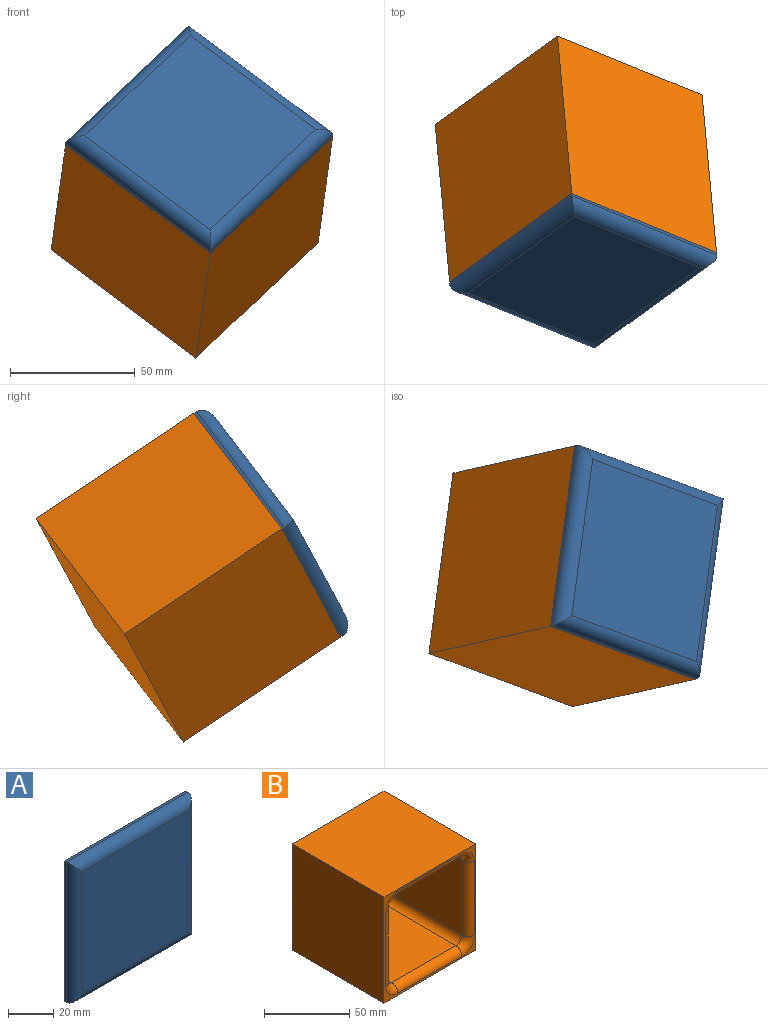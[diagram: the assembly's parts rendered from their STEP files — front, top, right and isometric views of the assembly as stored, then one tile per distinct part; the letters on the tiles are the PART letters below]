
ASSEMBLY  parts=2 mates=1
PART A: 10 faces, bbox 76.2x6.4x76.2 mm
  f0: plane 76.2x1.27mm, normal (0,0,-1), area 96.8mm2, adj f1,f3,f5,f6
  f1: plane 76.2x1.27mm, normal (1,0,0), area 96.8mm2, adj f0,f2,f5,f7
  f2: plane 76.2x1.27mm, normal (0,0,1), area 96.8mm2, adj f1,f3,f5,f9
  f3: plane 76.2x1.27mm, normal (-1,0,0), area 96.8mm2, adj f0,f2,f5,f8
  f4: plane 66.04x66.04mm, normal (0,-1,0), area 4361.3mm2, adj f6,f7,f8,f9
  f5: plane 76.2x76.2mm, normal (0,1,0), area 5806.4mm2, adj f0,f1,f2,f3
  f6: cylinder r=5.08mm len=76.2mm, axis (-1,0,0), area 578.6mm2, adj f0,f4,f7,f8
  f7: cylinder r=5.08mm len=76.2mm, axis (0,0,-1), area 578.6mm2, adj f1,f4,f6,f9
  f8: cylinder r=5.08mm len=76.2mm, axis (0,0,1), area 578.6mm2, adj f3,f4,f6,f9
  f9: cylinder r=5.08mm len=76.2mm, axis (1,0,0), area 578.6mm2, adj f2,f4,f7,f8
PART B: 31 faces, bbox 83.1x76.2x83.1 mm
  f0: plane 76.2x76.2mm, normal (0,-1,0), area 469.3mm2, adj f1,f2,f3,f4,f12,f15,f16,f19
  f1: plane 76.2x76.2mm, normal (1,0,0), area 5806.4mm2, adj f0,f2,f4,f5
  f2: plane 76.2x76.2mm, normal (0,0,1), area 5806.4mm2, adj f0,f1,f3,f5
  f3: plane 76.2x76.2mm, normal (-1,0,0), area 5806.4mm2, adj f0,f2,f4,f5
  f4: plane 76.2x76.2mm, normal (0,0,-1), area 5806.4mm2, adj f0,f1,f3,f5
  f5: plane 76.2x76.2mm, normal (0,1,0), area 5806.4mm2, adj f1,f2,f3,f4
  f6: plane 59.69x53.34mm, normal (0,0,1), area 3183.9mm2, adj f13,f17,f20,f21
  f7: plane 59.69x53.34mm, normal (-1,0,0), area 3183.9mm2, adj f18,f21,f24,f29
  f8: plane 59.69x53.34mm, normal (0,0,-1), area 3183.9mm2, adj f11,f14,f18,f19
  f9: plane 59.69x53.34mm, normal (1,0,0), area 3183.9mm2, adj f11,f12,f13,f26
  f10: plane 53.34x53.34mm, normal (0,-1,0), area 2845.2mm2, adj f14,f17,f26,f29
  f11: cylinder r=5.08mm len=59.69mm, axis (0,1,0), area 476.3mm2, adj f8,f9,f15,f27
  f12: cylinder r=5.08mm len=53.34mm, axis (0,0,1), area 425.6mm2, adj f0,f9,f15,f16
  f13: cylinder r=5.08mm len=59.69mm, axis (0,-1,0), area 476.3mm2, adj f6,f9,f16,f25
  f14: cylinder r=5.08mm len=53.34mm, axis (-1,0,0), area 425.6mm2, adj f8,f10,f27,f30
  f15: torus R=10.16mm, axis (0,-1,0), area 86.8mm2, adj f0,f11,f12,f19
  f16: torus R=10.16mm, axis (0,-1,0), area 86.8mm2, adj f0,f12,f13,f20
  f17: cylinder r=5.08mm len=53.34mm, axis (1,0,0), area 425.6mm2, adj f6,f10,f25,f28
  f18: cylinder r=5.08mm len=59.69mm, axis (0,-1,0), area 476.3mm2, adj f7,f8,f22,f30
  f19: cylinder r=5.08mm len=53.34mm, axis (1,0,0), area 425.6mm2, adj f0,f8,f15,f22
  f20: cylinder r=5.08mm len=53.34mm, axis (-1,0,0), area 425.6mm2, adj f0,f6,f16,f23
  f21: cylinder r=5.08mm len=59.69mm, axis (0,1,0), area 476.3mm2, adj f6,f7,f23,f28
  f22: torus R=10.16mm, axis (0,-1,0), area 86.8mm2, adj f0,f18,f19,f24
  f23: torus R=10.16mm, axis (0,-1,0), area 86.8mm2, adj f0,f20,f21,f24
  f24: cylinder r=5.08mm len=53.34mm, axis (0,0,-1), area 425.6mm2, adj f0,f7,f22,f23
  f25: sphere r=5.08mm, area 40.5mm2, adj f13,f17,f26
  f26: cylinder r=5.08mm len=53.34mm, axis (0,0,-1), area 425.6mm2, adj f9,f10,f25,f27
  f27: sphere r=5.08mm, area 40.5mm2, adj f11,f14,f26
  f28: sphere r=5.08mm, area 40.5mm2, adj f17,f21,f29
  f29: cylinder r=5.08mm len=53.34mm, axis (0,0,1), area 425.6mm2, adj f7,f10,f28,f30
  f30: sphere r=5.08mm, area 40.5mm2, adj f14,f18,f29
PLACE A rot(axis=(-0.64,0.76,-0.15),53.1deg) t=(-63.7,27.62,101.53)mm
PLACE B rot(axis=(-0.64,0.76,-0.15),53.1deg) t=(40.42,46.19,-22.69)mm
MATE revolute A.f0 <-> B.f4  axis (0.64,0.46,0.61) through (50.68,-46.53,-25.45)mm
